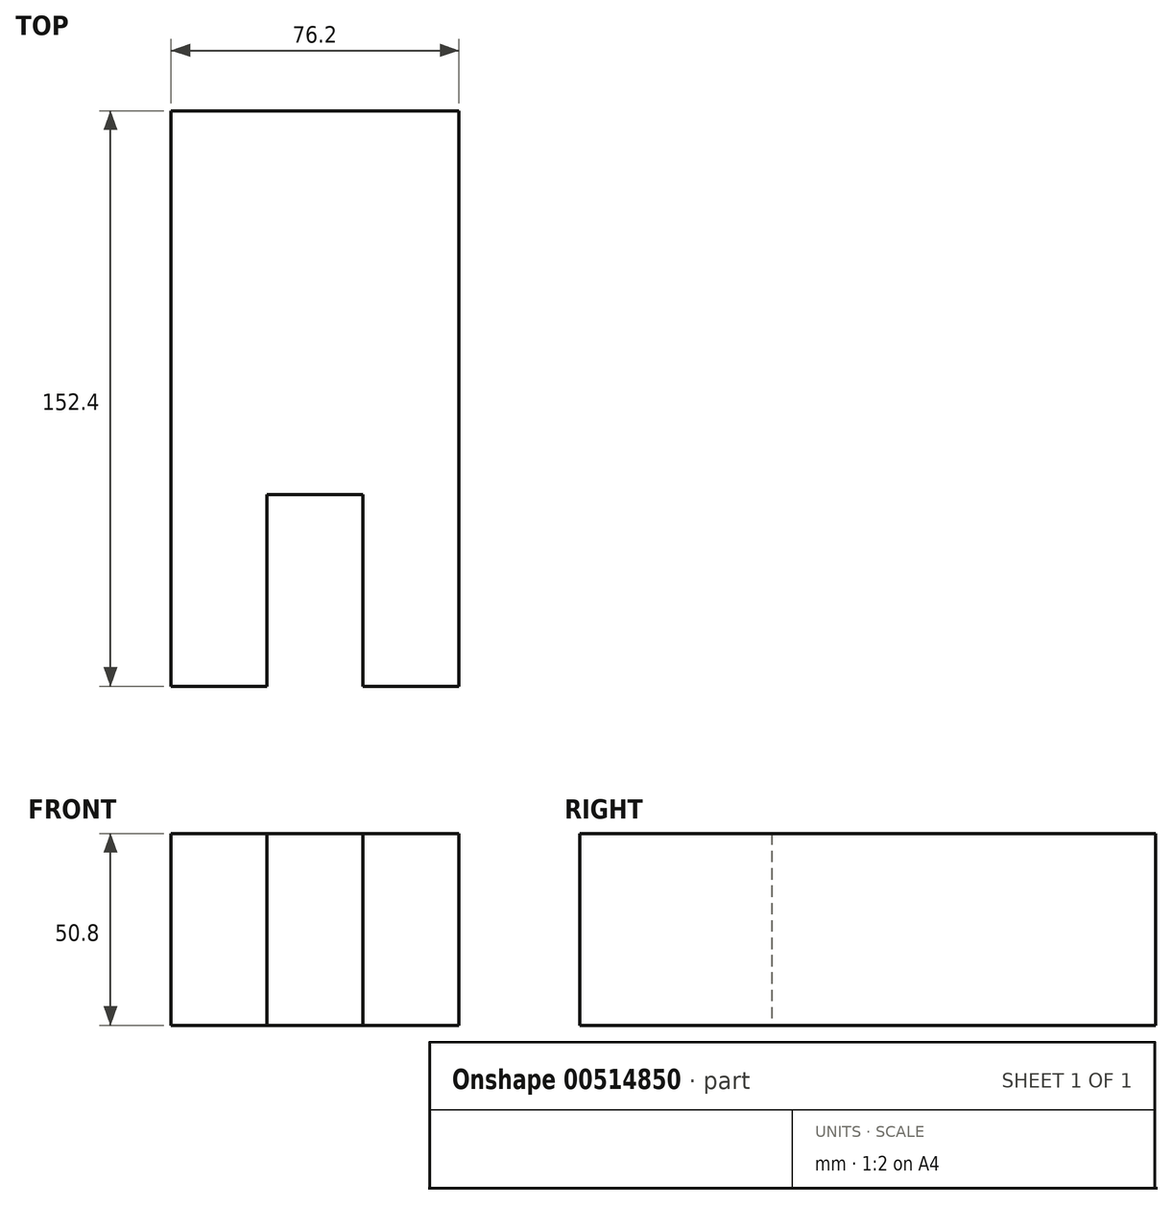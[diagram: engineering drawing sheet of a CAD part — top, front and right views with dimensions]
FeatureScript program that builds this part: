
annotation { "Feature Type Name" : "Feature", "Feature Type Description" : "" }
export const myFeature = defineFeature(function(context is Context, id is Id, definition is map)
    precondition{}
    {
        {
            var Q0;
            Q0=qCreatedBy(makeId("Top.planeOp"),FACE);
            var sketch = newSketch(context, id + "F0", { "sketchPlane" : qUnion([Q0])});
            skLineSegment(sketch, "E0", {"start": v(-38.06, 119.62) * mm, "end": v(-38.06, -32.78) * mm});
            skLineSegment(sketch, "E1", {"start": v(-38.06, -32.78) * mm, "end": v(-12.66, -32.78) * mm});
            skLineSegment(sketch, "E2", {"start": v(-12.66, -32.78) * mm, "end": v(-12.66, 18.02) * mm});
            skLineSegment(sketch, "E3", {"start": v(-12.66, 18.02) * mm, "end": v(12.74, 18.02) * mm});
            skLineSegment(sketch, "E4", {"start": v(12.74, 18.02) * mm, "end": v(12.74, -32.78) * mm});
            skLineSegment(sketch, "E5", {"start": v(12.74, -32.78) * mm, "end": v(38.14, -32.78) * mm});
            skLineSegment(sketch, "E6", {"start": v(38.14, -32.78) * mm, "end": v(38.14, 119.62) * mm});
            skLineSegment(sketch, "E7", {"start": v(38.14, 119.62) * mm, "end": v(-38.06, 119.62) * mm});
            skSolve(sketch);
        }
        {
            var Q0;
            Q0 = qSketchRegion(id + "F0", true);
            extrude(context, id + "F1", {"entities" : qUnion([Q0]), "depth" : 50.8 * mm, "offsetDistance" : 25.4 * mm});
        }
    });
